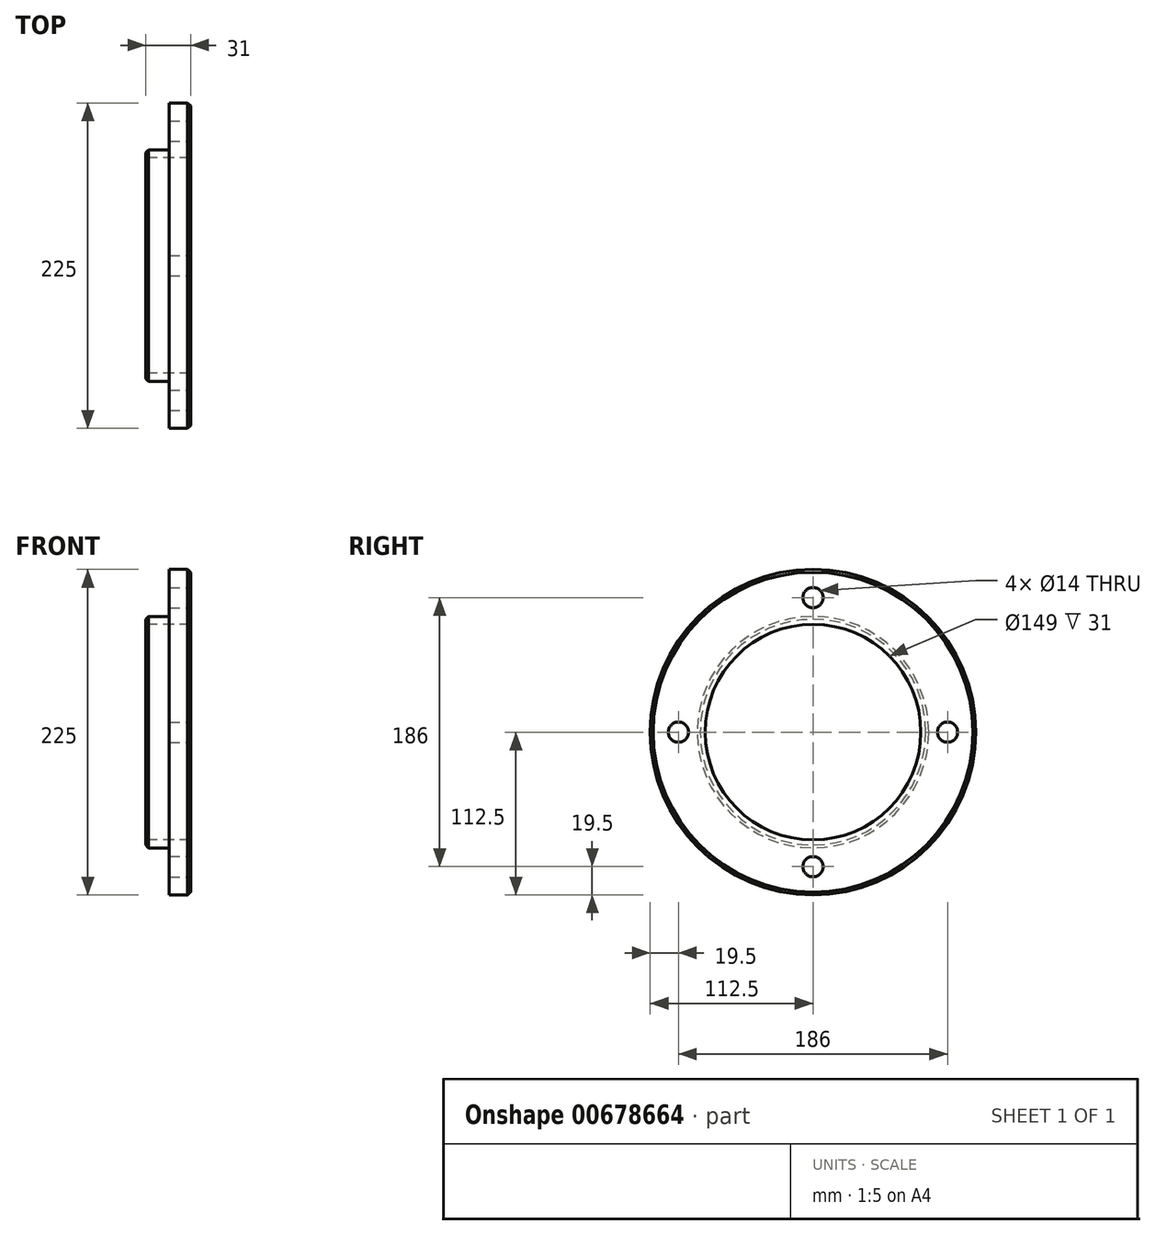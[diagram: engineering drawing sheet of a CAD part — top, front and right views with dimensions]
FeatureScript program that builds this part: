
annotation { "Feature Type Name" : "Feature", "Feature Type Description" : "" }
export const myFeature = defineFeature(function(context is Context, id is Id, definition is map)
    precondition{}
    {
        {
            var Q0;
            Q0=qCreatedBy(makeId("Right.planeOp"),FACE);
            var sketch = newSketch(context, id + "F0", { "sketchPlane" : qUnion([Q0])});
            skCircle(sketch, "E0", {"center": v(0, 0) * mm, "radius": 112.5 * mm});
            skSolve(sketch);
        }
        {
            var Q0;
            Q0 = qSketchRegion(id + "F0", true);
            extrude(context, id + "F1", {"entities" : qUnion([Q0]), "depth" : 14.9 * mm, "offsetDistance" : 25 * mm});
        }
        {
            var Q0;
            Q0=makeQuery(id+"F1.opExtrude","CAP_FACE",FACE,{"disambiguationData":[OSD([sQuery(id+"F0.wireOp",EDGE,"E0")])],"isStart":true});
            var sketch = newSketch(context, id + "F2", { "sketchPlane" : qUnion([Q0])});
            skCircle(sketch, "E1", {"center": v(0, 0) * mm, "radius": 80 * mm});
            skSolve(sketch);
        }
        {
            var Q0;
            Q0 = qSketchRegion(id + "F2", true);
            extrude(context, id + "F3", {"entities" : qUnion([Q0]), "operationType" : NewBodyOperationType.ADD, "depth" : 16.1 * mm, "offsetDistance" : 25 * mm});
        }
        {
            var Q0;
            Q0=makeQuery(id+"F3.opExtrude","CAP_EDGE",EDGE,{"disambiguationData":[OSD([sQuery(id+"F2.wireOp",EDGE,"E1")])],"isStart":false});
            var Q1;
            Q1=makeQuery(id+"F1.opExtrude","CAP_EDGE",EDGE,{"disambiguationData":[OSD([sQuery(id+"F0.wireOp",EDGE,"E0")])],"isStart":false});
            chamfer(context, id + "F4", {"entities" : qUnion([Q0, Q1]), "width" : 2 * mm, "tangentPropagation" : true});
        }
        {
            var Q0;
            Q0=makeQuery(id+"F3.opExtrude","CAP_FACE",FACE,{"disambiguationData":[OSD([sQuery(id+"F2.wireOp",EDGE,"E1")])],"isStart":false});
            var sketch = newSketch(context, id + "F5", { "sketchPlane" : qUnion([Q0])});
            skCircle(sketch, "E2", {"center": v(0, 0) * mm, "radius": 74.5 * mm});
            skSolve(sketch);
        }
        {
            var Q0;
            Q0 = qSketchRegion(id + "F5", true);
            extrude(context, id + "F6", {"entities" : qUnion([Q0]), "operationType" : NewBodyOperationType.REMOVE, "endBound" : BoundingType.THROUGH_ALL, "oppositeDirection" : true, "depth" : 25 * mm, "offsetDistance" : 25 * mm});
        }
        {
            var Q0;
            Q0=makeQuery(id+"F1.opExtrude","CAP_FACE",FACE,{"disambiguationData":[OSD([sQuery(id+"F0.wireOp",EDGE,"E0")])],"isStart":false});
            var sketch = newSketch(context, id + "F7", { "sketchPlane" : qUnion([Q0])});
            skCircle(sketch, "E3", {"center": v(0, 0) * mm, "radius": 93 * mm, "construction": true});
            skLineSegment(sketch, "E4", {"start": v(0, 0) * mm, "end": v(0, -93) * mm, "construction": true});
            skPoint(sketch, "E5", {"position": v(0, -93) * mm});
            skPoint(sketch, "E6.1.0", {"position": v(93, 0) * mm});
            skPoint(sketch, "E6.2.0", {"position": v(0, 93) * mm});
            skPoint(sketch, "E6.3.0", {"position": v(-93, 0) * mm});
            skSolve(sketch);
        }
        {
            var Q0;
            Q0=sQuery(id+"F7.wireOp",VERTEX,"E5");
            var Q1;
            Q1=sQuery(id+"F7.wireOp",VERTEX,"E6.3.0");
            var Q2;
            Q2=sQuery(id+"F7.wireOp",VERTEX,"E6.2.0");
            var Q3;
            Q3=sQuery(id+"F7.wireOp",VERTEX,"E6.1.0");
            var Q4;
            Q4=makeQuery(id+"F1.opExtrude","SWEPT_BODY",BODY,{"disambiguationData":[OSD([sQuery(id+"F0.wireOp",EDGE,"E0")])]});
            hole(context, id + "F8", {"style" : HoleStyle.SIMPLE, "endStyle" : HoleEndStyle.THROUGH, "holeDiameter" : 14 * mm, "majorDiameter" : 5 * mm, "isTappedThrough" : true, "tappedDepth" : 24.75 * mm, "tapClearance" : 3, "locations" : qUnion([Q0, Q1, Q2, Q3]), "scope" : qUnion([Q4])});
        }
    });
